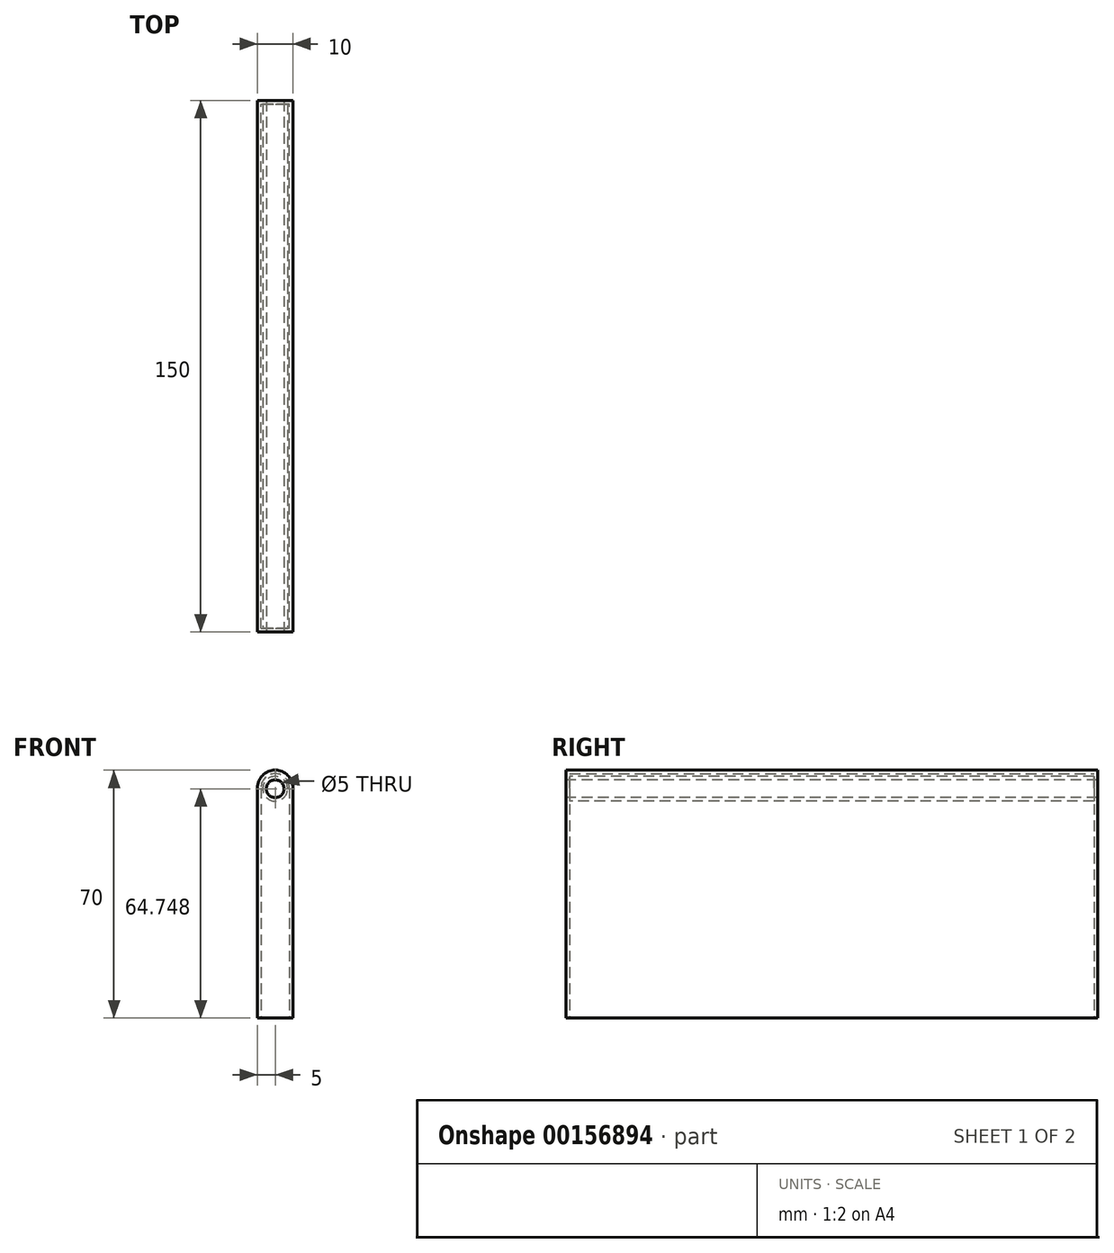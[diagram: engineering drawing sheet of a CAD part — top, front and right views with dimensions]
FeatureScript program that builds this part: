
annotation { "Feature Type Name" : "Feature", "Feature Type Description" : "" }
export const myFeature = defineFeature(function(context is Context, id is Id, definition is map)
    precondition{}
    {
        {
            var Q0;
            Q0=qCreatedBy(makeId("Right.planeOp"),FACE);
            var sketch = newSketch(context, id + "F0", { "sketchPlane" : qUnion([Q0])});
            skLineSegment(sketch, "E0.bottom", {"start": v(-75, 35) * mm, "end": v(75, 35) * mm});
            skLineSegment(sketch, "E0.top", {"start": v(-75, -35) * mm, "end": v(75, -35) * mm});
            skLineSegment(sketch, "E0.left", {"start": v(-75, 35) * mm, "end": v(-75, -35) * mm});
            skLineSegment(sketch, "E0.right", {"start": v(75, 35) * mm, "end": v(75, -35) * mm});
            skPoint(sketch, "E0.middle", {"position": v(0, 0) * mm});
            skSolve(sketch);
        }
        {
            var Q0;
            Q0 = qSketchRegion(id + "F0", true);
            extrude(context, id + "F1", {"entities" : qUnion([Q0]), "depth" : 10 * mm});
        }
        {
            var Q0;
            Q0=makeQuery(id+"F1.opExtrude","CAP_EDGE",EDGE,{"disambiguationData":[OSD([sQuery(id+"F0.wireOp",EDGE,"E0.bottom")])],"isStart":false});
            var Q1;
            Q1=makeQuery(id+"F1.opExtrude","CAP_EDGE",EDGE,{"disambiguationData":[OSD([sQuery(id+"F0.wireOp",EDGE,"E0.bottom")])],"isStart":true});
            fillet(context, id + "F2", {"entities" : qUnion([Q0, Q1]), "radius" : 5 * mm, "tangentPropagation" : true, "allowEdgeOverflow" : false});
        }
        {
            var Q0;
            Q0=qCreatedBy(makeId("Front.planeOp"),FACE);
            var sketch = newSketch(context, id + "F3", { "sketchPlane" : qUnion([Q0])});
            skLineSegment(sketch, "E1.0", {"start": v(10, -35) * mm, "end": v(0, -35) * mm, "construction": true});
            skLineSegment(sketch, "E2", {"start": v(5, -43.57) * mm, "end": v(5, 42.78) * mm, "construction": true});
            skPoint(sketch, "E2.startSnap0", {"position": v(5, -35) * mm});
            skCircle(sketch, "E3", {"center": v(5, 29.75) * mm, "radius": 2.5 * mm});
            skSolve(sketch);
        }
        {
            var Q0;
            Q0 = qSketchRegion(id + "F3", true);
            extrude(context, id + "F4", {"entities" : qUnion([Q0]), "operationType" : NewBodyOperationType.REMOVE, "endBound" : BoundingType.SYMMETRIC, "oppositeDirection" : true, "depth" : 161.5 * mm});
        }
        {
            var Q0;
            Q0=makeQuery(id+"F1.opExtrude","SWEPT_FACE",FACE,{"disambiguationData":[OSD([sQuery(id+"F0.wireOp",EDGE,"E0.top")])]});
            shell(context, id + "F5", {"entities" : qUnion([Q0]), "thickness" : 1 * mm});
        }
    });
